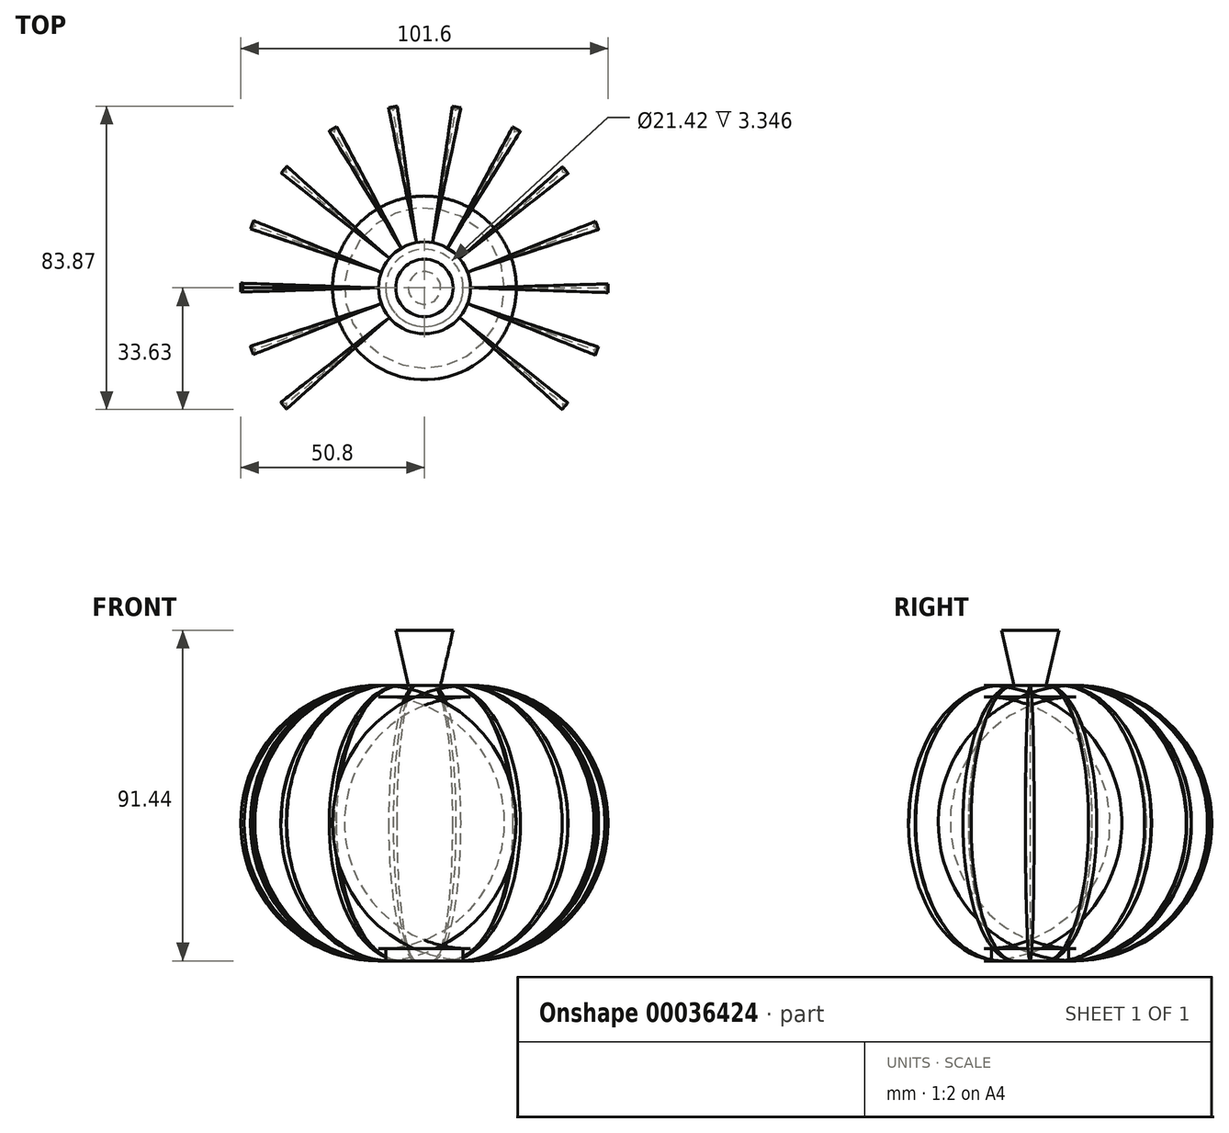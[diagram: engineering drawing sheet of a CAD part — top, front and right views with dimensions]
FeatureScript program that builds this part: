
annotation { "Feature Type Name" : "Feature", "Feature Type Description" : "" }
export const myFeature = defineFeature(function(context is Context, id is Id, definition is map)
    precondition{}
    {
        {
            var Q0;
            Q0=qCreatedBy(makeId("Front.planeOp"),FACE);
            var sketch = newSketch(context, id + "F0", { "sketchPlane" : qUnion([Q0])});
            skLineSegment(sketch, "E0.bottom", {"start": v(0, 0) * mm, "end": v(-12.7, 0) * mm});
            skLineSegment(sketch, "E0.top", {"start": v(0, 76.2) * mm, "end": v(-12.7, 76.2) * mm});
            skLineSegment(sketch, "E0.left", {"start": v(0, 0) * mm, "end": v(0, 76.2) * mm});
            skLineSegment(sketch, "E0.right", {"start": v(-12.7, 0) * mm, "end": v(-12.7, 76.2) * mm});
            skArc(sketch, "E1", {"start": v(-12.7, 76.2) * mm, "mid": v(-50.8, 38.1) * mm, "end": v(-12.7, 0) * mm});
            skArc(sketch, "E2", {"start": v(-12.7, 76.2) * mm, "mid": v(-49.9, 38.1) * mm, "end": v(-12.7, 0) * mm});
            skLineSegment(sketch, "E3", {"start": v(0, 73.03) * mm, "end": v(-12.7, 73.03) * mm});
            skArc(sketch, "E4", {"start": v(-12.7, 73.03) * mm, "mid": v(-47.54, 38.19) * mm, "end": v(-12.7, 3.35) * mm});
            skLineSegment(sketch, "E5", {"start": v(-12.7, 3.35) * mm, "end": v(0, 3.35) * mm});
            skSolve(sketch);
        }
        {
            var Q0;
            {var subQ2=sQuery(id+"F0.wireOp",EDGE,"E0.top");Q0=makeQuery(id+"F0.imprint","IMPRINT",FACE,{"disambiguationData":[TD([[makeQuery(id+"F0.imprint","IMPRINT",EDGE,{"derivedFrom":subQ2}),1.0]])]});}
            var Q1;
            {var subQ1=sQuery(id+"F0.wireOp",EDGE,"E2");Q1=makeQuery(id+"F0.imprint","IMPRINT",FACE,{"disambiguationData":[TD([[makeQuery(id+"F0.imprint","IMPRINT",EDGE,{"derivedFrom":subQ1}),1.0]])]});}
            var Q2;
            {var subQ2=sQuery(id+"F0.wireOp",EDGE,"E0.bottom");Q2=makeQuery(id+"F0.imprint","IMPRINT",FACE,{"disambiguationData":[TD([[makeQuery(id+"F0.imprint","IMPRINT",EDGE,{"derivedFrom":subQ2}),-1.0]])]});}
            var Q3;
            Q3=makeQuery(id+"F0.imprint","IMPRINT",FACE,{"disambiguationData":[TD([[makeQuery(id+"F0.imprint","IMPRINT",EDGE,{"derivedFrom":sQuery(id+"F0.wireOp",EDGE,"E1")}),1.0]])]});
            var Q4;
            Q4=sQuery(id+"F0.wireOp",EDGE,"E0.left");
            revolve(context, id + "F1", {"entities" : qUnion([Q0, Q1, Q2, Q3]), "axis" : qUnion([Q4]), "revolveType" : RevolveType.FULL});
        }
        {
            var Q0;
            Q0=qCreatedBy(makeId("Right.planeOp"),FACE);
            cPlane(context, id + "F2", {"entities" : qUnion([Q0]), "cplaneType" : CPlaneType.OFFSET, "offset" : 12.7 * mm, "oppositeDirection" : true, "width" : 152.4 * mm, "height" : 152.4 * mm});
        }
        {
            var Q0;
            Q0=qCreatedBy(id+"F2.planeOp",FACE);
            var sketch = newSketch(context, id + "F3", { "sketchPlane" : qUnion([Q0])});
            skLineSegment(sketch, "E6", {"start": v(0, 76.2) * mm, "end": v(-4.57, 79.8) * mm});
            skLineSegment(sketch, "E7", {"start": v(-4.57, 79.8) * mm, "end": v(5.32, 79.8) * mm});
            skLineSegment(sketch, "E8", {"start": v(5.32, 79.8) * mm, "end": v(0, 76.2) * mm});
            skSolve(sketch);
        }
        {
            var Q0;
            Q0=makeQuery(id+"F3.imprint","IMPRINT",FACE,{"disambiguationData":[TD([[makeQuery(id+"F3.imprint","IMPRINT",EDGE,{"derivedFrom":sQuery(id+"F3.wireOp",EDGE,"E6")}),-1.0]])]});
            var Q1;
            Q1=sQuery(id+"F0.wireOp",EDGE,"E2");
            sweep(context, id + "F4", {"operationType" : NewBodyOperationType.REMOVE, "profiles" : qUnion([Q0]), "path" : qUnion([Q1])});
        }
        {
            var Q0;
            Q0=makeQuery(id+"F4.boolean.opBoolean","COPY",FACE,{"derivedFrom":makeQuery(id+"F4.opSweep","SWEPT_FACE",FACE,{"disambiguationData":[OSD([sQuery(id+"F0.wireOp",EDGE,"E2"),sQuery(id+"F3.wireOp",EDGE,"E8")])]})});
            var Q1;
            Q1=makeQuery(id+"F4.boolean.opBoolean","COPY",FACE,{"derivedFrom":makeQuery(id+"F4.opSweep","SWEPT_FACE",FACE,{"disambiguationData":[OSD([sQuery(id+"F0.wireOp",EDGE,"E2"),sQuery(id+"F3.wireOp",EDGE,"E6")])]})});
            var Q2;
            Q2=sQuery(id+"F0.wireOp",EDGE,"E0.left");
            circularPattern(context, id + "F5", {"faces" : qUnion([Q0, Q1]), "axis" : qUnion([Q2]), "angle" : 360 * degree, "instanceCount" : round(18), "equalSpace" : true, "patternType" : PatternType.FACE});
        }
        {
            var Q0;
            Q0=makeQuery(id+"F1.opRevolve","SWEPT_FACE",FACE,{"disambiguationData":[OSD([sQuery(id+"F0.wireOp",EDGE,"E0.bottom")])]});
            var sketch = newSketch(context, id + "F6", { "sketchPlane" : qUnion([Q0])});
            skCircle(sketch, "E9", {"center": v(0, 0) * mm, "radius": 10.7 * mm});
            skSolve(sketch);
        }
        {
            var Q0;
            Q0=makeQuery(id+"F6.imprint","IMPRINT",FACE,{"disambiguationData":[TD([[makeQuery(id+"F6.imprint","IMPRINT",EDGE,{"derivedFrom":sQuery(id+"F6.wireOp",EDGE,"E9")}),1.0]])]});
            extrude(context, id + "F7", {"entities" : qUnion([Q0]), "operationType" : NewBodyOperationType.REMOVE, "oppositeDirection" : true, "depth" : 25.4 * mm});
        }
        {
            var Q0;
            Q0=qCreatedBy(makeId("Front.planeOp"),FACE);
            cPlane(context, id + "F8", {"entities" : qUnion([Q0]), "cplaneType" : CPlaneType.OFFSET, "offset" : 76.2 * mm, "width" : 152.4 * mm, "height" : 152.4 * mm});
        }
        {
            var Q0;
            Q0=qCreatedBy(id+"F8.planeOp",FACE);
            var sketch = newSketch(context, id + "F9", { "sketchPlane" : qUnion([Q0])});
            skLineSegment(sketch, "E10", {"start": v(0, 47.04) * mm, "end": v(15.24, 47.04) * mm, "construction": true});
            skLineSegment(sketch, "E11", {"start": v(0, 47.04) * mm, "end": v(-15.24, 47.04) * mm, "construction": true});
            skLineSegment(sketch, "E12", {"start": v(0, 47.04) * mm, "end": v(0, 33.54) * mm, "construction": true});
            skLineSegment(sketch, "E13", {"start": v(15.24, 47.04) * mm, "end": v(30.48, 47.04) * mm});
            skLineSegment(sketch, "E14", {"start": v(30.48, 47.04) * mm, "end": v(30.48, 57.2) * mm});
            skLineSegment(sketch, "E15", {"start": v(30.48, 57.2) * mm, "end": v(15.24, 47.04) * mm});
            skLineSegment(sketch, "E16", {"start": v(-15.24, 47.04) * mm, "end": v(-30.48, 47.04) * mm});
            skLineSegment(sketch, "E17", {"start": v(-30.48, 47.04) * mm, "end": v(-30.48, 57.2) * mm});
            skLineSegment(sketch, "E18", {"start": v(-30.48, 57.2) * mm, "end": v(-15.24, 47.04) * mm});
            skLineSegment(sketch, "E19", {"start": v(0, 33.54) * mm, "end": v(3.47, 26.49) * mm});
            skLineSegment(sketch, "E20", {"start": v(3.47, 26.49) * mm, "end": v(6.13, 33.54) * mm});
            skLineSegment(sketch, "E21", {"start": v(6.13, 33.54) * mm, "end": v(8.4, 26.49) * mm});
            skLineSegment(sketch, "E22", {"start": v(8.4, 26.49) * mm, "end": v(11.56, 33.94) * mm});
            skLineSegment(sketch, "E23", {"start": v(11.56, 33.94) * mm, "end": v(14.97, 26.74) * mm});
            skLineSegment(sketch, "E24", {"start": v(14.97, 26.74) * mm, "end": v(17.88, 34.45) * mm});
            skLineSegment(sketch, "E25", {"start": v(17.88, 34.45) * mm, "end": v(19.78, 34.45) * mm});
            skArc(sketch, "E26", {"start": v(18.51, 16.75) * mm, "mid": v(22.93, 25.33) * mm, "end": v(19.78, 34.45) * mm});
            skLineSegment(sketch, "E27", {"start": v(18.51, 16.75) * mm, "end": v(15.73, 16.75) * mm});
            skLineSegment(sketch, "E28", {"start": v(15.73, 16.75) * mm, "end": v(12.45, 23.83) * mm});
            skLineSegment(sketch, "E29", {"start": v(12.45, 23.83) * mm, "end": v(9.16, 16.75) * mm});
            skLineSegment(sketch, "E30", {"start": v(9.16, 16.75) * mm, "end": v(6.13, 24.34) * mm});
            skLineSegment(sketch, "E31", {"start": v(6.13, 24.34) * mm, "end": v(2.84, 16.75) * mm});
            skLineSegment(sketch, "E32", {"start": v(2.84, 16.75) * mm, "end": v(0, 24.34) * mm});
            skLineSegment(sketch, "E33.MirrorCS", {"start": v(-17.88, 34.45) * mm, "end": v(-19.78, 34.45) * mm});
            skLineSegment(sketch, "E34.MirrorCS", {"start": v(-18.51, 16.75) * mm, "end": v(-15.73, 16.75) * mm});
            skLineSegment(sketch, "E35.MirrorCS", {"start": v(-12.45, 23.83) * mm, "end": v(-9.16, 16.75) * mm});
            skLineSegment(sketch, "E36.MirrorCS", {"start": v(-6.13, 24.34) * mm, "end": v(-2.84, 16.75) * mm});
            skLineSegment(sketch, "E37.MirrorCS", {"start": v(-11.56, 33.94) * mm, "end": v(-14.97, 26.74) * mm});
            skLineSegment(sketch, "E38.MirrorCS", {"start": v(-9.16, 16.75) * mm, "end": v(-6.13, 24.34) * mm});
            skLineSegment(sketch, "E39.MirrorCS", {"start": v(-2.84, 16.75) * mm, "end": v(0, 24.34) * mm});
            skLineSegment(sketch, "E40.MirrorCS", {"start": v(-8.4, 26.49) * mm, "end": v(-11.56, 33.94) * mm});
            skLineSegment(sketch, "E41.MirrorCS", {"start": v(-6.13, 33.54) * mm, "end": v(-8.4, 26.49) * mm});
            skLineSegment(sketch, "E42.MirrorCS", {"start": v(-14.97, 26.74) * mm, "end": v(-17.88, 34.45) * mm});
            skLineSegment(sketch, "E43.MirrorCS", {"start": v(-3.47, 26.49) * mm, "end": v(-6.13, 33.54) * mm});
            skLineSegment(sketch, "E44.MirrorCS", {"start": v(0, 33.54) * mm, "end": v(-3.47, 26.49) * mm});
            skLineSegment(sketch, "E45.MirrorCS", {"start": v(-15.73, 16.75) * mm, "end": v(-12.45, 23.83) * mm});
            skArc(sketch, "E46.MirrorCS", {"start": v(-18.51, 16.75) * mm, "mid": v(-22.93, 25.33) * mm, "end": v(-19.78, 34.45) * mm});
            skLineSegment(sketch, "E47.MirrorCS", {"start": v(0, 47.04) * mm, "end": v(0, 33.54) * mm});
            skSolve(sketch);
        }
        {
            var Q0;
            Q0=makeQuery(id+"F9.imprint","IMPRINT",FACE,{"disambiguationData":[TD([[makeQuery(id+"F9.imprint","IMPRINT",EDGE,{"derivedFrom":sQuery(id+"F9.wireOp",EDGE,"E19")}),-1.0]])]});
            var Q1;
            Q1=makeQuery(id+"F9.imprint","IMPRINT",FACE,{"disambiguationData":[TD([[makeQuery(id+"F9.imprint","IMPRINT",EDGE,{"derivedFrom":sQuery(id+"F9.wireOp",EDGE,"E16")}),-1.0]])]});
            var Q2;
            Q2=makeQuery(id+"F9.imprint","IMPRINT",FACE,{"disambiguationData":[TD([[makeQuery(id+"F9.imprint","IMPRINT",EDGE,{"derivedFrom":sQuery(id+"F9.wireOp",EDGE,"E13")}),1.0]])]});
            extrude(context, id + "F10", {"entities" : qUnion([Q0, Q1, Q2]), "operationType" : NewBodyOperationType.REMOVE, "oppositeDirection" : true, "depth" : 50.8 * mm});
        }
        {
            var Q0;
            Q0=makeQuery(id+"F1.opRevolve","SWEPT_FACE",FACE,{"disambiguationData":[OSD([sQuery(id+"F0.wireOp",EDGE,"E0.top")])]});
            var sketch = newSketch(context, id + "F11", { "sketchPlane" : qUnion([Q0])});
            skCircle(sketch, "E48", {"center": v(0, 0) * mm, "radius": 4.48 * mm});
            skSolve(sketch);
        }
        {
            var Q0;
            Q0=makeQuery(id+"F11.imprint","IMPRINT",FACE,{"disambiguationData":[TD([[makeQuery(id+"F11.imprint","IMPRINT",EDGE,{"derivedFrom":sQuery(id+"F11.wireOp",EDGE,"E48")}),-1.0]])]});
            cPlane(context, id + "F12", {"entities" : qUnion([Q0]), "cplaneType" : CPlaneType.OFFSET, "offset" : 15.24 * mm, "width" : 152.4 * mm, "height" : 152.4 * mm});
        }
        {
            var Q0;
            Q0=qCreatedBy(id+"F12.planeOp",FACE);
            var sketch = newSketch(context, id + "F13", { "sketchPlane" : qUnion([Q0])});
            skCircle(sketch, "E49", {"center": v(0, 0) * mm, "radius": 7.94 * mm});
            skSolve(sketch);
        }
        {
            var Q1;
            Q1=makeQuery(id+"F13.imprint","IMPRINT",FACE,{"disambiguationData":[TD([[makeQuery(id+"F13.imprint","IMPRINT",EDGE,{"derivedFrom":sQuery(id+"F13.wireOp",EDGE,"E49")}),1.0]])]});
            var Q2;
            Q2=makeQuery(id+"F11.imprint","IMPRINT",FACE,{"disambiguationData":[TD([[makeQuery(id+"F11.imprint","IMPRINT",EDGE,{"derivedFrom":sQuery(id+"F11.wireOp",EDGE,"E48")}),1.0]])]});
            loft(context, id + "F14", {"operationType" : NewBodyOperationType.ADD, "sheetProfilesArray" : [{ "sheetProfileEntities" : qUnion([Q1]) }, { "sheetProfileEntities" : qUnion([Q2]) }]});
        }
    });
